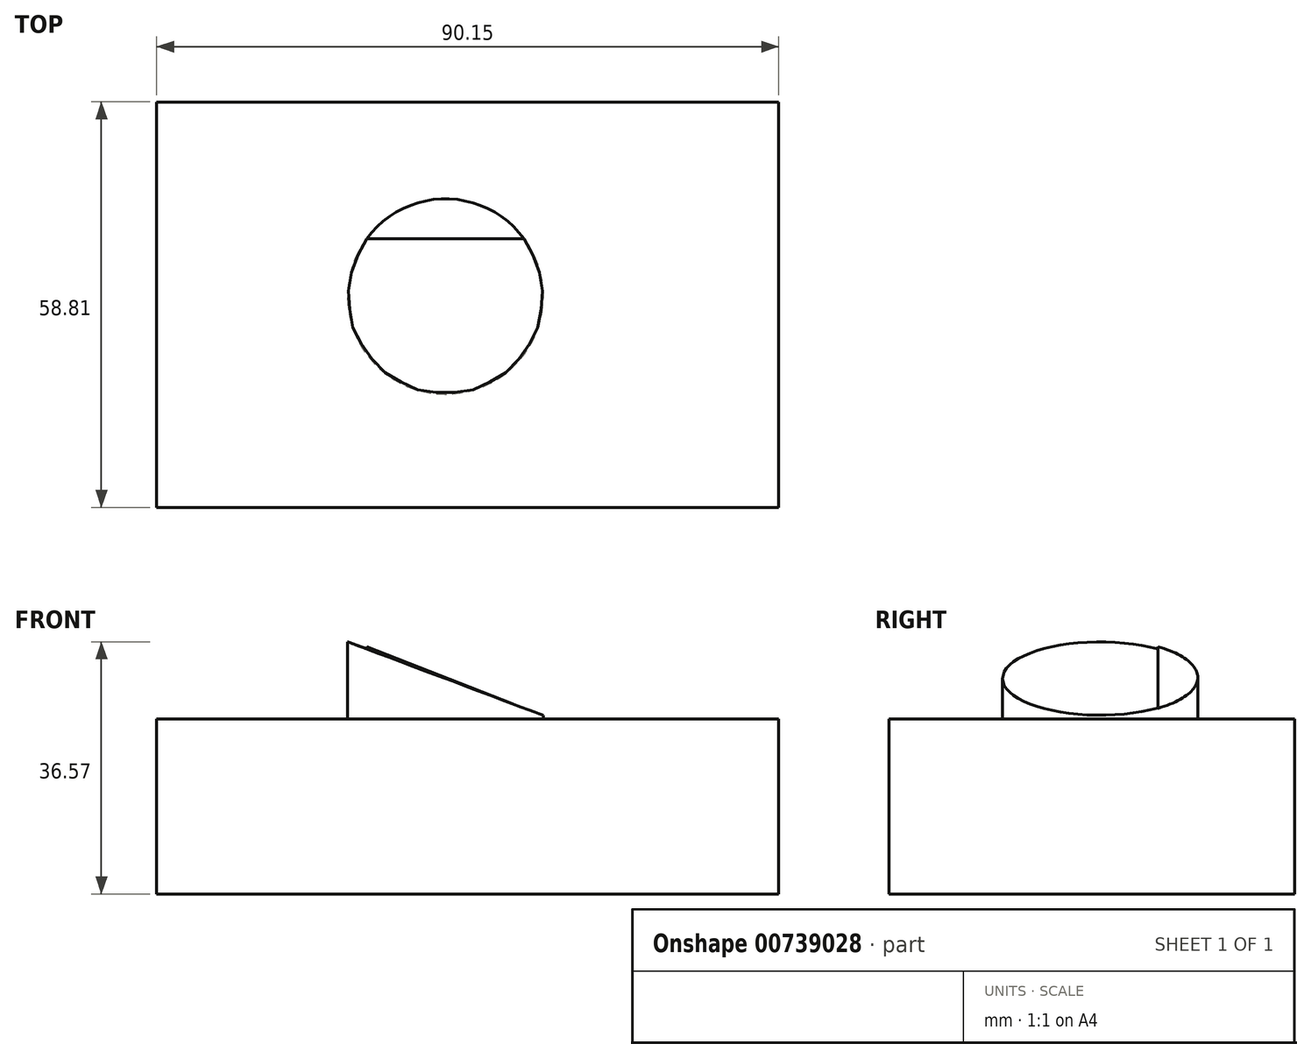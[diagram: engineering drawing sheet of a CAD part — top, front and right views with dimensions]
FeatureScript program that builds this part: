
annotation { "Feature Type Name" : "Feature", "Feature Type Description" : "" }
export const myFeature = defineFeature(function(context is Context, id is Id, definition is map)
    precondition{}
    {
        {
            var Q0;
            Q0=qCreatedBy(makeId("Top.planeOp"),FACE);
            var sketch = newSketch(context, id + "F0", { "sketchPlane" : qUnion([Q0])});
            skLineSegment(sketch, "E0.bottom", {"start": v(-40.1, 19.82) * mm, "end": v(50.05, 19.82) * mm});
            skLineSegment(sketch, "E0.top", {"start": v(-40.1, -39) * mm, "end": v(50.05, -39) * mm});
            skLineSegment(sketch, "E0.left", {"start": v(-40.1, 19.82) * mm, "end": v(-40.1, -39) * mm});
            skLineSegment(sketch, "E0.right", {"start": v(50.05, 19.82) * mm, "end": v(50.05, -39) * mm});
            skSolve(sketch);
        }
        {
            var Q0;
            Q0 = qSketchRegion(id + "F0", true);
            extrude(context, id + "F1", {"entities" : qUnion([Q0]), "depth" : 25.4 * mm, "offsetDistance" : 25.4 * mm});
        }
        {
            var Q0;
            Q0=qCreatedBy(makeId("Top.planeOp"),FACE);
            var sketch = newSketch(context, id + "F2", { "sketchPlane" : qUnion([Q0])});
            skCircle(sketch, "E1", {"center": v(1.75, -8.39) * mm, "radius": 14.17 * mm});
            skSolve(sketch);
        }
        {
            var Q0;
            Q0 = qSketchRegion(id + "F2", true);
            extrude(context, id + "F3", {"entities" : qUnion([Q0]), "operationType" : NewBodyOperationType.ADD, "depth" : 38.1 * mm, "offsetDistance" : 25.4 * mm});
        }
        {
            var Q0;
            Q0=qCreatedBy(makeId("Front.planeOp"),FACE);
            var sketch = newSketch(context, id + "F4", { "sketchPlane" : qUnion([Q0])});
            skLineSegment(sketch, "E2", {"start": v(-27.2, 42.13) * mm, "end": v(15.95, 25.9) * mm});
            skLineSegment(sketch, "E3", {"start": v(15.95, 25.9) * mm, "end": v(15.95, 45.63) * mm});
            skLineSegment(sketch, "E4", {"start": v(15.95, 45.63) * mm, "end": v(-27.2, 42.13) * mm});
            skSolve(sketch);
        }
        {
            var Q0;
            Q0 = qSketchRegion(id + "F4", true);
            extrude(context, id + "F5", {"entities" : qUnion([Q0]), "operationType" : NewBodyOperationType.REMOVE, "depth" : 261.37 * mm, "offsetDistance" : 25.4 * mm});
        }
        {
            var Q0;
            Q0=qCreatedBy(makeId("Front.planeOp"),FACE);
            var sketch = newSketch(context, id + "F6", { "sketchPlane" : qUnion([Q0])});
            skLineSegment(sketch, "E5", {"start": v(-12.44, 36.96) * mm, "end": v(15.76, 25.9) * mm});
            skLineSegment(sketch, "E6", {"start": v(15.76, 25.9) * mm, "end": v(15.76, 43.97) * mm});
            skLineSegment(sketch, "E7", {"start": v(15.76, 43.97) * mm, "end": v(-12.63, 43.97) * mm});
            skLineSegment(sketch, "E8", {"start": v(-12.63, 43.97) * mm, "end": v(-12.44, 36.96) * mm});
            skSolve(sketch);
        }
        {
            var Q0;
            Q0 = qSketchRegion(id + "F6", true);
            extrude(context, id + "F7", {"entities" : qUnion([Q0]), "operationType" : NewBodyOperationType.REMOVE, "oppositeDirection" : true, "depth" : 25.4 * mm, "offsetDistance" : 25.4 * mm});
        }
    });
